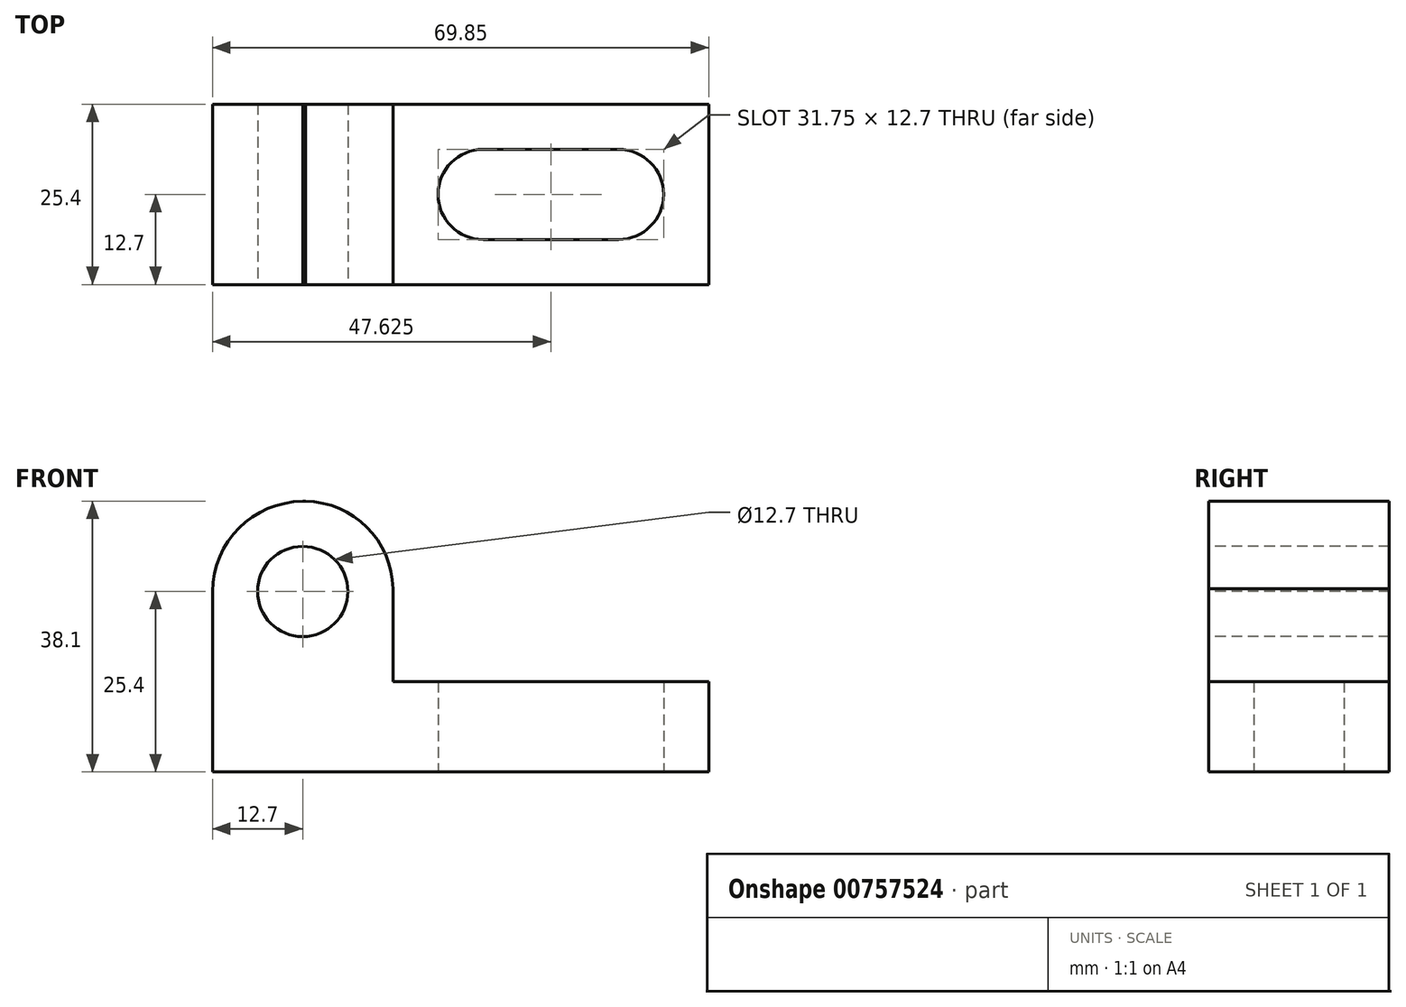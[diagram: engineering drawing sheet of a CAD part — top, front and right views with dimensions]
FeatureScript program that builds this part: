
annotation { "Feature Type Name" : "Feature", "Feature Type Description" : "" }
export const myFeature = defineFeature(function(context is Context, id is Id, definition is map)
    precondition{}
    {
        {
            var Q0;
            Q0=qCreatedBy(makeId("Front.planeOp"),FACE);
            var sketch = newSketch(context, id + "F0", { "sketchPlane" : qUnion([Q0])});
            skLineSegment(sketch, "E0", {"start": v(0, 0) * mm, "end": v(0, 38.1) * mm});
            skLineSegment(sketch, "E1", {"start": v(0, 38.1) * mm, "end": v(25.4, 38.1) * mm});
            skLineSegment(sketch, "E2", {"start": v(25.4, 38.1) * mm, "end": v(25.4, 12.7) * mm});
            skLineSegment(sketch, "E3", {"start": v(25.4, 12.7) * mm, "end": v(69.85, 12.7) * mm});
            skLineSegment(sketch, "E4", {"start": v(69.85, 12.7) * mm, "end": v(69.85, 0) * mm});
            skLineSegment(sketch, "E5", {"start": v(69.85, 0) * mm, "end": v(0, 0) * mm});
            skSolve(sketch);
        }
        {
            var Q0;
            Q0 = qSketchRegion(id + "F0", true);
            extrude(context, id + "F1", {"entities" : qUnion([Q0]), "depth" : 25.4 * mm, "offsetDistance" : 25.4 * mm});
        }
        {
            var Q0;
            Q0=makeQuery(id+"F1.opExtrude","CAP_FACE",FACE,{"disambiguationData":[OSD([sQuery(id+"F0.wireOp",EDGE,"E0"),sQuery(id+"F0.wireOp",EDGE,"E1"),sQuery(id+"F0.wireOp",EDGE,"E2"),sQuery(id+"F0.wireOp",EDGE,"E3"),sQuery(id+"F0.wireOp",EDGE,"E4"),sQuery(id+"F0.wireOp",EDGE,"E5")])],"isStart":false});
            var sketch = newSketch(context, id + "F2", { "sketchPlane" : qUnion([Q0])});
            skLineSegment(sketch, "E6", {"start": v(0, 25.4) * mm, "end": v(25.4, 25.4) * mm});
            skCircle(sketch, "E7", {"center": v(12.7, 25.4) * mm, "radius": 6.35 * mm});
            skSolve(sketch);
        }
        {
            var Q0;
            {var subQ0=sQuery(id+"F2.wireOp",EDGE,"E7");var subQ1=sQuery(id+"F2.wireOp",EDGE,"E6");var subQ2=makeQuery(id+"F2.imprint","INTERSECT",VERTEX,{"disambiguationData":[OD(0.0)],"derivedFrom":[subQ1,subQ0]});Q0=makeQuery(id+"F2.imprint","IMPRINT",FACE,{"disambiguationData":[TD([[makeQuery(id+"F2.imprint","IMPRINT",EDGE,{"disambiguationData":[TD([[subQ2,-1.0]])],"derivedFrom":subQ1}),1.0]])]});}
            var Q1;
            {var subQ0=sQuery(id+"F2.wireOp",EDGE,"E7");var subQ1=sQuery(id+"F2.wireOp",EDGE,"E6");var subQ2=makeQuery(id+"F2.imprint","INTERSECT",VERTEX,{"disambiguationData":[OD(0.0)],"derivedFrom":[subQ1,subQ0]});Q1=makeQuery(id+"F2.imprint","IMPRINT",FACE,{"disambiguationData":[TD([[makeQuery(id+"F2.imprint","IMPRINT",EDGE,{"disambiguationData":[TD([[subQ2,-1.0]])],"derivedFrom":subQ1}),-1.0]])]});}
            extrude(context, id + "F3", {"entities" : qUnion([Q0, Q1]), "operationType" : NewBodyOperationType.REMOVE, "endBound" : BoundingType.THROUGH_ALL, "oppositeDirection" : true, "depth" : 25.4 * mm, "offsetDistance" : 25.4 * mm});
        }
        {
            var Q0;
            Q0=makeQuery(id+"F1.opExtrude","CAP_FACE",FACE,{"disambiguationData":[OSD([sQuery(id+"F0.wireOp",EDGE,"E0"),sQuery(id+"F0.wireOp",EDGE,"E1"),sQuery(id+"F0.wireOp",EDGE,"E2"),sQuery(id+"F0.wireOp",EDGE,"E3"),sQuery(id+"F0.wireOp",EDGE,"E4"),sQuery(id+"F0.wireOp",EDGE,"E5")])],"isStart":false});
            var sketch = newSketch(context, id + "F4", { "sketchPlane" : qUnion([Q0])});
            skArc(sketch, "E8", {"start": v(25.4, 25.4) * mm, "mid": v(21.74, 34.44) * mm, "end": v(12.7, 38.1) * mm});
            skArc(sketch, "E9", {"start": v(12.7, 38.1) * mm, "mid": v(3.76, 34.34) * mm, "end": v(0, 25.4) * mm});
            skSolve(sketch);
        }
        {
            var Q0;
            {var subQ0=sQuery(id+"F4.wireOp",EDGE,"E9");Q0=makeQuery(id+"F4.imprint","IMPRINT",FACE,{"disambiguationData":[TD([[makeQuery(id+"F4.imprint","IMPRINT",EDGE,{"derivedFrom":subQ0}),-1.0]])]});}
            var Q1;
            {var subQ0=sQuery(id+"F4.wireOp",EDGE,"E8");var subQ1=makeQuery(id+"F1.opExtrude","CAP_EDGE",EDGE,{"disambiguationData":[OSD([sQuery(id+"F0.wireOp",EDGE,"E2")])],"isStart":false});var subQ2=makeQuery(id+"F4.imprint","INTERSECT",VERTEX,{"disambiguationData":[OD(1.0)],"derivedFrom":[subQ1,subQ0]});Q1=makeQuery(id+"F4.imprint","IMPRINT",FACE,{"disambiguationData":[TD([[makeQuery(id+"F4.imprint","IMPRINT",EDGE,{"disambiguationData":[TD([[subQ2,-1.0]])],"derivedFrom":subQ0}),-1.0]])]});}
            extrude(context, id + "F5", {"entities" : qUnion([Q0, Q1]), "operationType" : NewBodyOperationType.REMOVE, "endBound" : BoundingType.THROUGH_ALL, "oppositeDirection" : true, "depth" : 25.4 * mm, "offsetDistance" : 25.4 * mm});
        }
        {
            var Q0;
            Q0=makeQuery(id+"F1.opExtrude","SWEPT_FACE",FACE,{"disambiguationData":[OSD([sQuery(id+"F0.wireOp",EDGE,"E5")])]});
            var sketch = newSketch(context, id + "F6", { "sketchPlane" : qUnion([Q0])});
            skLineSegment(sketch, "E10", {"start": v(63.5, 12.7) * mm, "end": v(63.5, 12.7) * mm});
            skLineSegment(sketch, "E11", {"start": v(57.15, 6.35) * mm, "end": v(38.1, 6.35) * mm});
            skLineSegment(sketch, "E12", {"start": v(31.75, 12.7) * mm, "end": v(31.75, 12.7) * mm});
            skLineSegment(sketch, "E13", {"start": v(38.1, 19.05) * mm, "end": v(57.15, 19.05) * mm});
            skPoint(sketch, "E14.visualSharp", {"position": v(63.5, 19.05) * mm});
            skArc(sketch, "E14.filletArc", {"start": v(63.5, 12.7) * mm, "mid": v(61.64, 17.2) * mm, "end": v(57.15, 19.05) * mm});
            skPoint(sketch, "E15.visualSharp", {"position": v(63.5, 6.35) * mm});
            skArc(sketch, "E15.filletArc", {"start": v(57.15, 6.35) * mm, "mid": v(61.64, 8.2) * mm, "end": v(63.5, 12.7) * mm});
            skPoint(sketch, "E16.visualSharp", {"position": v(31.75, 6.35) * mm});
            skArc(sketch, "E16.filletArc", {"start": v(31.75, 12.7) * mm, "mid": v(33.6, 8.2) * mm, "end": v(38.1, 6.35) * mm});
            skPoint(sketch, "E17.visualSharp", {"position": v(31.75, 19.05) * mm});
            skArc(sketch, "E17.filletArc", {"start": v(38.1, 19.05) * mm, "mid": v(33.6, 17.2) * mm, "end": v(31.75, 12.7) * mm});
            skSolve(sketch);
        }
        {
            var Q0;
            Q0 = qSketchRegion(id + "F6", true);
            extrude(context, id + "F7", {"entities" : qUnion([Q0]), "operationType" : NewBodyOperationType.REMOVE, "endBound" : BoundingType.THROUGH_ALL, "oppositeDirection" : true, "depth" : 25.4 * mm, "offsetDistance" : 25.4 * mm});
        }
    });
